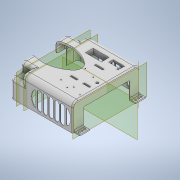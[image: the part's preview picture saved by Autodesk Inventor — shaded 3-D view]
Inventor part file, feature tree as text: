
AUTODESK INVENTOR PART (.ipt)
format: ipt  version: 2020 (Build 240168000, 168)  size: 1,326,080 bytes
history: native  units: in
note: dims shown in document units (in); Inventor stores cm internally (conversion verified against a paired STEP export)
features: extrude x25, projected_geometry x23, sketch x20, fillet x11, plane x8, mirror x4, thicken_offset x2, shell x1, pattern_linear x1, hole x1, other x1
ambient origin geometry x8: Origin, YZ Plane, XZ Plane, XY Plane, X Axis, Y Axis, Z Axis, Center Point
bodies: Solid1 (feature_tree)
feature tree (97):
  extrude  "Extrusion1"  Depth=3.189in
  shell  "Shell1"  Thickness=6.8701in
  thicken_offset  "Thicken1"
  thicken_offset  "Thicken2"
  extrude  "Extrusion3"  Depth=2.7559in TaperAngle=0.0deg
  extrude  "Extrusion4"  Depth=0.125in TaperAngle=0.0deg
  plane  "Work Plane1"
  mirror  "Mirror1"
  mirror  "Mirror2"
  extrude  "Extrusion8"  Depth=1.0in
  extrude  "Extrusion9"  Depth=0.1875in
  pattern_linear  "Rectangular Pattern2"  Count1=2 Spacing1=0.2756in
  mirror  "Mirror3"
  extrude  "Extrusion10"  Depth=0.125in
  fillet  "Fillet1"  Radius=4.1732in
  fillet  "Fillet2"  Radius=2.2904in
  extrude  "Extrusion11"  Depth=0.125in
  extrude  "Extrusion12"  Depth=0.125in
  fillet  "Fillet7"  Radius=1.1811in
  fillet  "Fillet8"  Radius=1.159in
  extrude  "Extrusion13"  Depth=0.125in TaperAngle=0.0deg
  extrude  "Extrusion32"  Depth=0.125in
  extrude  "Extrusion40"  Depth=0.125in
  hole  "Hole1"  [1 undecoded]
  plane  "Work Plane2"
  extrude  "Extrusion14"  Depth=0.125in
  plane  "Work Plane3"
  extrude  "Extrusion15"  Depth=0.125in
  plane  "Work Plane4"
  extrude  "Extrusion16"  Depth=0.3937in
  extrude  "Extrusion17"  Depth=0.125in TaperAngle=0.0deg
  fillet  "Fillet9"  Radius=0.9449in
  extrude  "Extrusion18"  Depth=0.125in TaperAngle=0.0deg
  plane  "Work Plane5"
  extrude  "Extrusion19"  Depth=0.125in
  fillet  "Fillet13"  Radius=0.5in
  plane  "Work Plane8"
  sketch  "Sketch23"  dims[d42=0.1875in]
  extrude  "Extrusion21"  Depth=0.125in
  mirror  "Mirror4"
  extrude  "Extrusion33"  Depth=0.125in
  extrude  "Extrusion34"  Depth=0.125in
  extrude  "Extrusion35"  Depth=0.125in
  extrude  "Extrusion36"  Depth=0.125in
  extrude  "Extrusion37"  Depth=0.125in
  extrude  "Extrusion38"  Depth=0.125in
  extrude  "Extrusion39"  Depth=0.125in
  fillet  "Fillet24"  Radius=0.1575in
  fillet  "Fillet25"  Radius=0.1575in
  fillet  "Fillet26"  Radius=0.857in
  fillet  "Fillet27"  Radius=0.5in
  fillet  "Fillet28"  Radius=0.1378in
  sketch  "Sketch1"  dims[d0=4.7244in d1=3.189in d2=6.8701in]
  sketch  "Sketch3"  dims[d4=5.3543in d5=2.7559in d6=0.0in]
  projected_geometry  "Projected Loop3"
  projected_geometry  "Projected Loop4"
  sketch  "Sketch9"  dims[d7=0.1969in d12=0.125in d13=0.0in]
  projected_geometry  "Projected Loop9"
  sketch  "Sketch10"  dims[d18=0.815in d19=1.0in]
  projected_geometry  "Projected Loop10"
  sketch  "Sketch11"  dims[d20=1.0in d21=0.1875in]
  projected_geometry  "Projected Loop11"
  sketch  "Sketch12"  dims[d22=0.1875in]
  projected_geometry  "Projected Loop12"
  sketch  "Sketch13"  dims[d23=0.1875in]
  projected_geometry  "Projected Loop13"
  projected_geometry  "Projected Loop14"
  sketch  "Sketch16"  dims[d24=0.125in d25=0.0in]
  projected_geometry  "Projected Loop15"
  projected_geometry  "Projected Loop16"
  sketch  "Sketch17"  dims[d40=1.0236in]
  projected_geometry  "Projected Loop17"
  projected_geometry  "Projected Loop18"
  projected_geometry  "Projected Loop19"
  sketch  "Sketch21"  dims[d41=0.1875in]
  other  "Work Axis1"
  plane  "Work Plane6"
  plane  "Work Plane7"
  projected_geometry  "Projected Loop22"
  sketch  "Sketch31"  dims[d43=0.1875in]
  sketch  "Sketch35"  dims[d44=0.815in]
  sketch  "Sketch36"  dims[d45=1.0in]
  projected_geometry  "Projected Loop43"
  sketch  "Sketch37"  dims[d46=1.0in]
  projected_geometry  "Projected Loop44"
  projected_geometry  "Projected Loop45"
  sketch  "Sketch38"  dims[d47=0.5236in]
  projected_geometry  "Projected Loop46"
  sketch  "Sketch39"  dims[d48=0.3937in d49=0.0in]
  projected_geometry  "Projected Loop47"
  sketch  "Sketch40"  dims[d50=0.1575in]
  projected_geometry  "Projected Loop48"
  projected_geometry  "Projected Loop49"
  sketch  "Sketch41"  dims[d51=0.3937in d52=0.0in d53=0.7874in d55=0.2756in]
  projected_geometry  "Projected Loop50"
  projected_geometry  "Projected Loop51"
  sketch  "Sketch42"  dims[d56=0.7874in d58=0.2756in d59=0.125in d60=4.1732in d61=2.2904in d62=1.7717in d63=2.1654in d64=1.1811in d66=1.159in d67=0.8661in d68=0.0in d69=0.1in d70=1.8898in d71=0.145in d72=0.45in d80=0.225in d81=1.9685in d83=0.59in d84=0.3937in d86=1.0in d88=1.0in d89=0.0in d90=0.9449in d91=1.0in d92=0.0in d107=0.68in d108=0.5in d109=0.1378in d110=0.1378in d111=0.1575in d112=0.1575in d114=0.68in d115=0.5in d120=0.1378in d121=0.1378in d122=0.1575in d123=0.1575in d128=0.857in d129=0.5in d130=0.1378in d131=0.1378in d132=0.1575in d133=0.1575in d135=0.2559in d137=1.5in d146=0.1988in d147=0.3209in d148=0.1575in d149=0.1378in d152=0.68in d153=0.1575in d154=1.1811in d155=0.68in d156=0.1575in d157=1.1811in d158=0.857in d159=0.1575in d160=1.1811in d161=1.0in d162=0.0in d163=0.4724in d164=0.4528in d165=1.1811in d166=0.15in d167=0.1575in d168=0.0831in d170=0.125in d171=0.125in d172=2.2in d173=0.0in d174=0.9843in d175=0.0in d177=1.1024in d178=1.1024in d179=0.0591in d180=0.0in d182=1.378in d183=0.5906in d184=0.0591in d185=0.0in d186=0.125in d188=2.9134in d190=1.6929in d191=1.5748in d192=1.3561in d193=0.3839in d194=1.3824in d195=1.0075in d196=1.2051in d198=0.0591in d199=0.0in d200=0.0591in d201=0.0in d205=0.1168in d208=0.125in d209=0.9843in d210=1.3386in d211=90.0deg d212=5.8046in d213=-0.7874in d214=1.2598in d215=0.9055in d216=0.9843in d217=0.0in d256=0.1378in d283=0.1378in d290=0.0689in d291=0.0689in d292=0.0689in d293=0.0689in d294=0.0689in d295=0.0689in d296=0.125in d297=0.0in d298=0.0968in d299=0.1in d300=0.375in d301=0.25in d302=0.5635in d303=0.346in d304=0.8108in d307=0.8661in d308=0.0in d309=0.0591in d310=0.0in d311=0.0591in d312=0.0in d313=0.0591in d314=0.0in d315=0.0591in d316=0.0in d317=0.7559in d318=5.8046in d319=0.854in d320=5.8046in d321=0.9843in d322=0.0in d323=0.5in d324=0.35in d325=0.049in d326=0.0in d327=0.35in d328=0.05in d329=0.125in d330=0.8in d331=1.65in d332=2.0in d333=1.0in d334=0.15in d335=0.375in d336=0.0in d337=0.1476in d338=0.1476in d339=0.1476in d340=0.1476in d10=0.5in d11=0.0344in d222=0.5in d223=0.0344in d224=0.5in d225=0.0344in]
note: 1 required parameter value undecoded (feature->parameter linkage not recoverable at this tier; creation-order binding heuristic only, values carry confidence <= 0.55)
